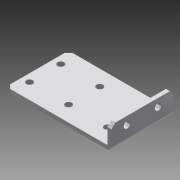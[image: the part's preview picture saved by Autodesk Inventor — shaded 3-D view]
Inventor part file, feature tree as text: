
AUTODESK INVENTOR PART (.ipt)
format: ipt  version: 2016 SP1 (Build 200210100, 210)  size: 107,520 bytes
history: native  units: in
note: dims shown in document units (in); Inventor stores cm internally (conversion verified against a paired STEP export)
features: chamfer x1
ambient origin geometry x8: Origin, YZ Plane, XZ Plane, XY Plane, X Axis, Y Axis, Z Axis, Center Point
bodies: Solid1 (feature_tree)
feature tree (1):
  chamfer  "Chamfer2"  [1 undecoded]
note: 1 required parameter value undecoded (feature->parameter linkage not recoverable at this tier; creation-order binding heuristic only, values carry confidence <= 0.55)
